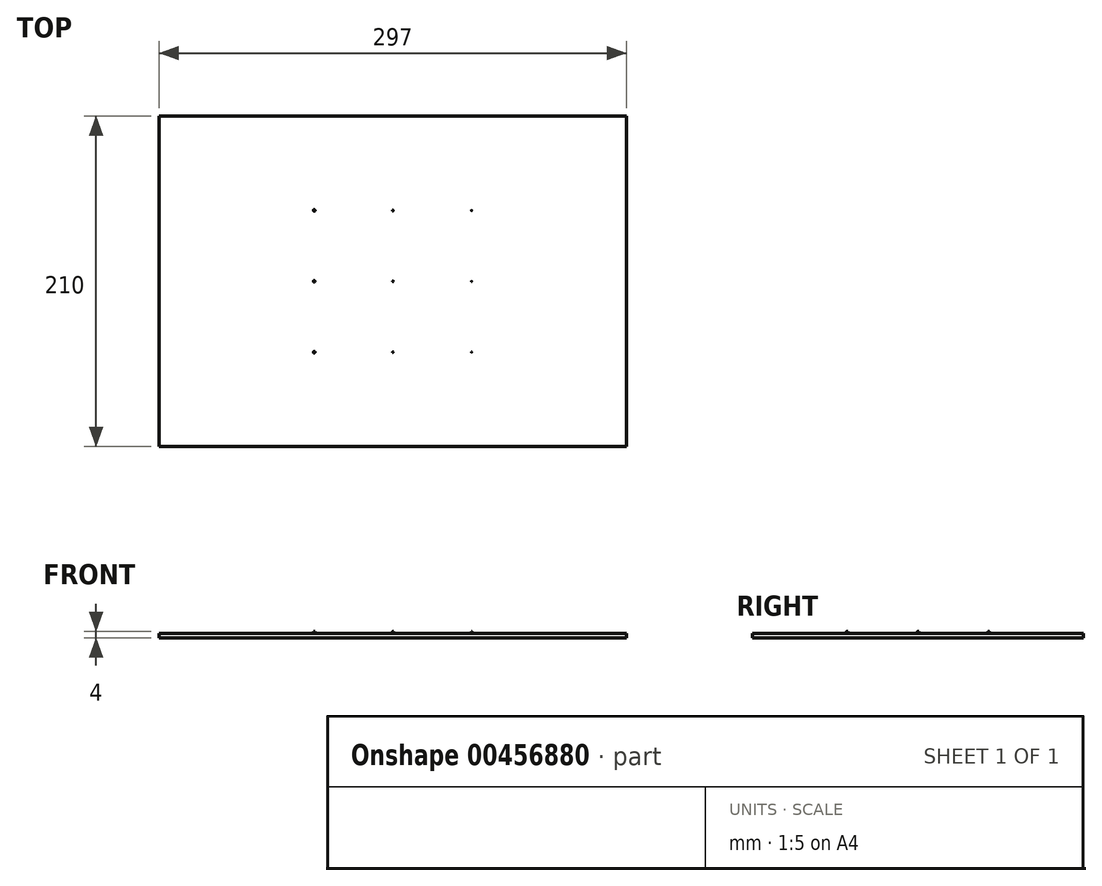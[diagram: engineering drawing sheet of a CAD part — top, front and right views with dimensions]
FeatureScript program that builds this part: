
annotation { "Feature Type Name" : "Feature", "Feature Type Description" : "" }
export const myFeature = defineFeature(function(context is Context, id is Id, definition is map)
    precondition{}
    {
        {
            var Q0;
            Q0=qCreatedBy(makeId("Top.planeOp"),FACE);
            var sketch = newSketch(context, id + "F0", { "sketchPlane" : qUnion([Q0])});
            skLineSegment(sketch, "E0.bottom", {"start": v(-148.5, 105) * mm, "end": v(148.5, 105) * mm});
            skLineSegment(sketch, "E0.top", {"start": v(-148.5, -105) * mm, "end": v(148.5, -105) * mm});
            skLineSegment(sketch, "E0.left", {"start": v(-148.5, 105) * mm, "end": v(-148.5, -105) * mm});
            skLineSegment(sketch, "E0.right", {"start": v(148.5, 105) * mm, "end": v(148.5, -105) * mm});
            skPoint(sketch, "E0.middle", {"position": v(0, 0) * mm});
            skSolve(sketch);
        }
        {
            var Q0;
            Q0=qSketchRegion(id+"F0",true);
            extrude(context, id + "F1", {"entities" : qUnion([Q0]), "depth" : 3 * mm});
        }
        {
            var Q0;
            Q0=makeQuery(id+"F1.opExtrude","CAP_FACE",FACE,{"disambiguationData":[OSD([sQuery(id+"F0.wireOp",EDGE,"E0.bottom"),sQuery(id+"F0.wireOp",EDGE,"E0.top"),sQuery(id+"F0.wireOp",EDGE,"E0.left"),sQuery(id+"F0.wireOp",EDGE,"E0.right")])],"isStart":false});
            var sketch = newSketch(context, id + "F2", { "sketchPlane" : qUnion([Q0])});
            skCircle(sketch, "E1", {"center": v(50, 45) * mm, "radius": 0.1 * mm});
            skCircle(sketch, "E2", {"center": v(50, 0) * mm, "radius": 0.1 * mm});
            skCircle(sketch, "E3", {"center": v(50, -45) * mm, "radius": 0.1 * mm});
            skSolve(sketch);
        }
        {
            var Q0;
            Q0=qSketchRegion(id+"F2",true);
            extrude(context, id + "F3", {"entities" : qUnion([Q0]), "operationType" : NewBodyOperationType.ADD, "depth" : 1 * mm});
        }
        {
            var Q0;
            Q0=makeQuery(id+"F1.opExtrude","CAP_FACE",FACE,{"disambiguationData":[OSD([sQuery(id+"F0.wireOp",EDGE,"E0.bottom"),sQuery(id+"F0.wireOp",EDGE,"E0.top"),sQuery(id+"F0.wireOp",EDGE,"E0.left"),sQuery(id+"F0.wireOp",EDGE,"E0.right")])],"isStart":false});
            var sketch = newSketch(context, id + "F4", { "sketchPlane" : qUnion([Q0])});
            skCircle(sketch, "E4", {"center": v(0, 45) * mm, "radius": 0.25 * mm});
            skCircle(sketch, "E5", {"center": v(0, 0) * mm, "radius": 0.25 * mm});
            skCircle(sketch, "E6", {"center": v(0, -45) * mm, "radius": 0.25 * mm});
            skSolve(sketch);
        }
        {
            var Q0;
            Q0=qSketchRegion(id+"F4",true);
            extrude(context, id + "F5", {"entities" : qUnion([Q0]), "operationType" : NewBodyOperationType.ADD, "depth" : 1 * mm});
        }
        {
            var Q0;
            Q0=makeQuery(id+"F1.opExtrude","CAP_FACE",FACE,{"disambiguationData":[OSD([sQuery(id+"F0.wireOp",EDGE,"E0.bottom"),sQuery(id+"F0.wireOp",EDGE,"E0.top"),sQuery(id+"F0.wireOp",EDGE,"E0.left"),sQuery(id+"F0.wireOp",EDGE,"E0.right")])],"isStart":false});
            var sketch = newSketch(context, id + "F6", { "sketchPlane" : qUnion([Q0])});
            skCircle(sketch, "E7", {"center": v(-50, 45) * mm, "radius": 0.5 * mm});
            skCircle(sketch, "E8", {"center": v(-50, 0) * mm, "radius": 0.5 * mm});
            skCircle(sketch, "E9", {"center": v(-50, -45) * mm, "radius": 0.5 * mm});
            skSolve(sketch);
        }
        {
            var Q0;
            Q0=qSketchRegion(id+"F6",true);
            extrude(context, id + "F7", {"entities" : qUnion([Q0]), "operationType" : NewBodyOperationType.ADD, "depth" : 1 * mm});
        }
    });
